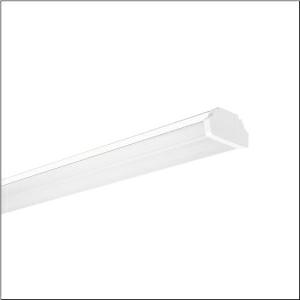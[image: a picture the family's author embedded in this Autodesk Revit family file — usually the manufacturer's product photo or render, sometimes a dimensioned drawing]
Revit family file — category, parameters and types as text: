
# Revit family: dus_31_gen_2_53bd812mv4fxd2_7d94
name_source: partatom
category: Lighting Fixtures
units: mm (PartAtom-declared; Revit-internal decimal feet)

## family parameters
Cut with Voids When Loaded = No
Host = Face
Light Source = No
Part Type = Normal
Room Calculation Point = No
Round Connector Dimension = Use Diameter
Shared = No

## types (1)
- --- (1 x LED, 15440 lm, 82.3 W, 4000K)
    Apparent Load = 82 VA
    CIE Flux Codes = 47 80 95 93 100
    Color Rendering = 80
    Color Temperature = 4000K
    Default Elevation = 1800 mm
    Description = DUS 31 Gen.2, luminaire insert, of sheet steel, coil coated, white, length: 1.535mm, width: 81mm, height: 90mm, 5x system unit, system units: 307mm, LED rated luminous flux: 15.440lm, light colour: 840, SDCM (Standard Deviation of Colour Matching)MacAdam ≤ 3 SDCM (initial), control gear: ON/OFF Multilumen, control gear: ECG, with plug, 3-pole, with phase selection, mains connection: 220..240V, AC, 50/60Hz, rated input power: 82W, through-wiring accessed according to module size, primary optical cover: cover, of PMMA, light emission: direct distribution, primary light characteristic: symmetric, protection rating (complete): IP20, protection rating (LED compartment): IP50, insulation class (complete): insulation class I (protective earthing), certification: CE, ENEC, VDE, UKCA, impact resistance: IK03, permissible ambient temperature for indoor applications: -35..+35°C, corresponds to IFS (International Featured Standards) requirements for safety and quality in the food industry, reducing of maximum allowable ambient temperature of 5°C with ceiling mounting, packaging unit: 1 piece
    Height = 95 mm
    Lamp = 1 x LED
    Lamp Light Flux = 15440 lm
    Lamp Power = 82.3 W
    Lamp count = 1
    Length = 1535 mm
    Luminous efficacy = 188 lm/W
    Manufacturer = Siteco
    ModVariant = No
    Model = 53BD812MV4FXD2
    Mounting Place = Ceiling
    Mounting Type = Pendant
    Number of Poles = 1
    OnlyDefault = Yes
    Power Factor = 1
    Product Name = DUS 31 Gen.2
    Product group = luminaire insert | ceiling pendant
    ProductGroupID = 901
    Protection Class = Protection class I
    Protection Degree = IP 20
    RLX_Detail_Level = 1
    RLX_Emergency_Light_Flux = 0 lm
    RLX_Emergency_Type = 0
    RLX_Emergency_Type_DB = No
    RlxData = <blob elided: 29805 chars, md5=bb5fb24b>
    Socket = socket
    Standby Power = 0 W
    System Light Flux = 15440 lm
    System Power = 82 W
    Type Comments = factory setting: luminous flux: 100 % | (A | C | E) | 193 mA
    Type Image = l_1319596.jpg
    URL = http://relux.com
    VarID = @adj_051269
    Voltage = 0 V
    Weight = 0.00 kg
    Width = 81 mm

## geometry (parser evidence)
native form markers: Blend x4, Sweep x11
no freeform markers — native parametric forms only
